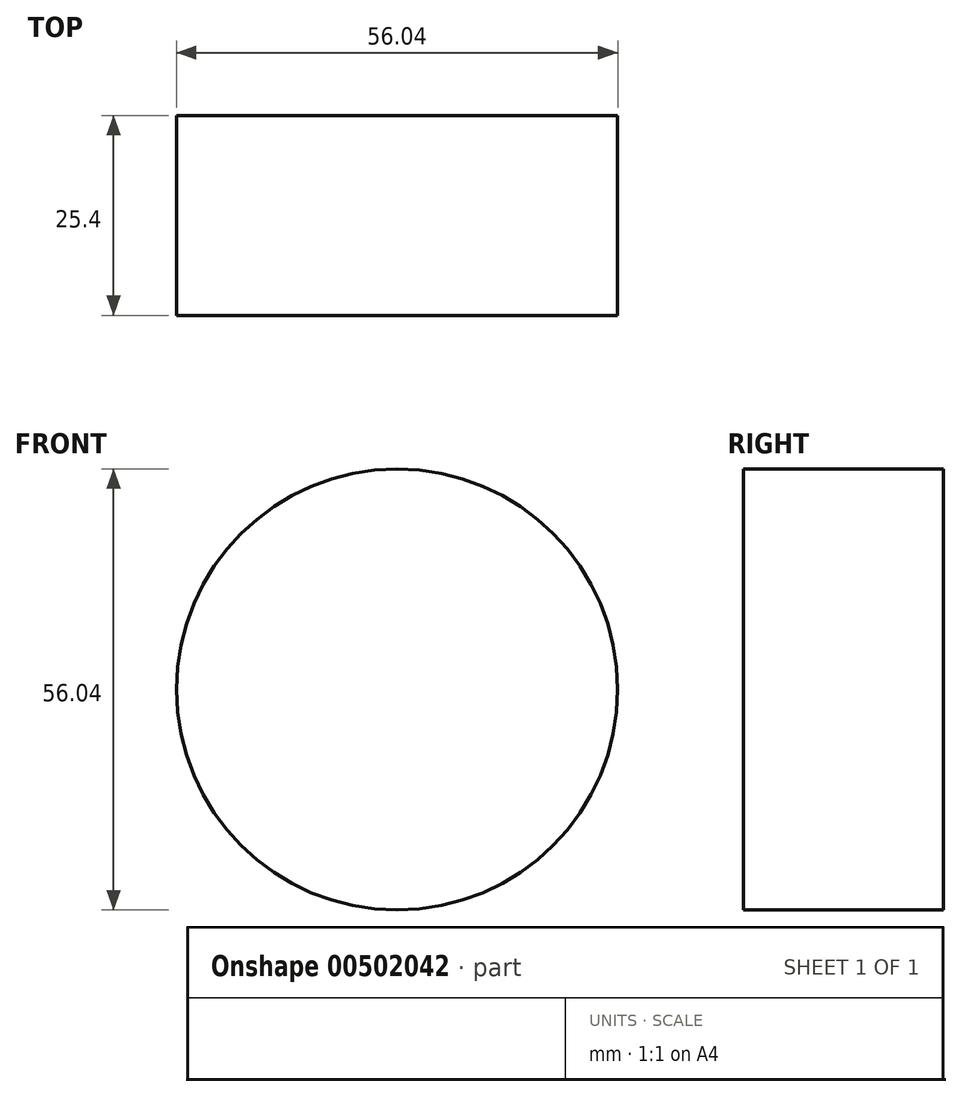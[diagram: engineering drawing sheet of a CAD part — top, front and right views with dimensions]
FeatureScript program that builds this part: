
annotation { "Feature Type Name" : "Feature", "Feature Type Description" : "" }
export const myFeature = defineFeature(function(context is Context, id is Id, definition is map)
    precondition{}
    {
        {
            var Q0;
            Q0=qCreatedBy(makeId("Front.planeOp"),FACE);
            var sketch = newSketch(context, id + "F0", { "sketchPlane" : qUnion([Q0])});
            skCircle(sketch, "E0", {"center": v(0, 0) * mm, "radius": 28.02 * mm});
            skSolve(sketch);
        }
        {
            var Q0;
            Q0=makeQuery(id+"F0.imprint","IMPRINT",FACE,{"disambiguationData":[TD([[makeQuery(id+"F0.imprint","IMPRINT",EDGE,{"derivedFrom":sQuery(id+"F0.wireOp",EDGE,"E0")}),1.0]])]});
            extrude(context, id + "F1", {"entities" : qUnion([Q0]), "depth" : 127 * mm});
        }
        {
            var Q0;
            Q0=makeQuery(id+"F1.opExtrude","CAP_FACE",FACE,{"disambiguationData":[OSD([sQuery(id+"F0.wireOp",EDGE,"E0")])],"isStart":false});
            extrude(context, id + "F2", {"entities" : qUnion([Q0]), "operationType" : NewBodyOperationType.INTERSECT, "oppositeDirection" : true, "depth" : 25.4 * mm});
        }
    });
